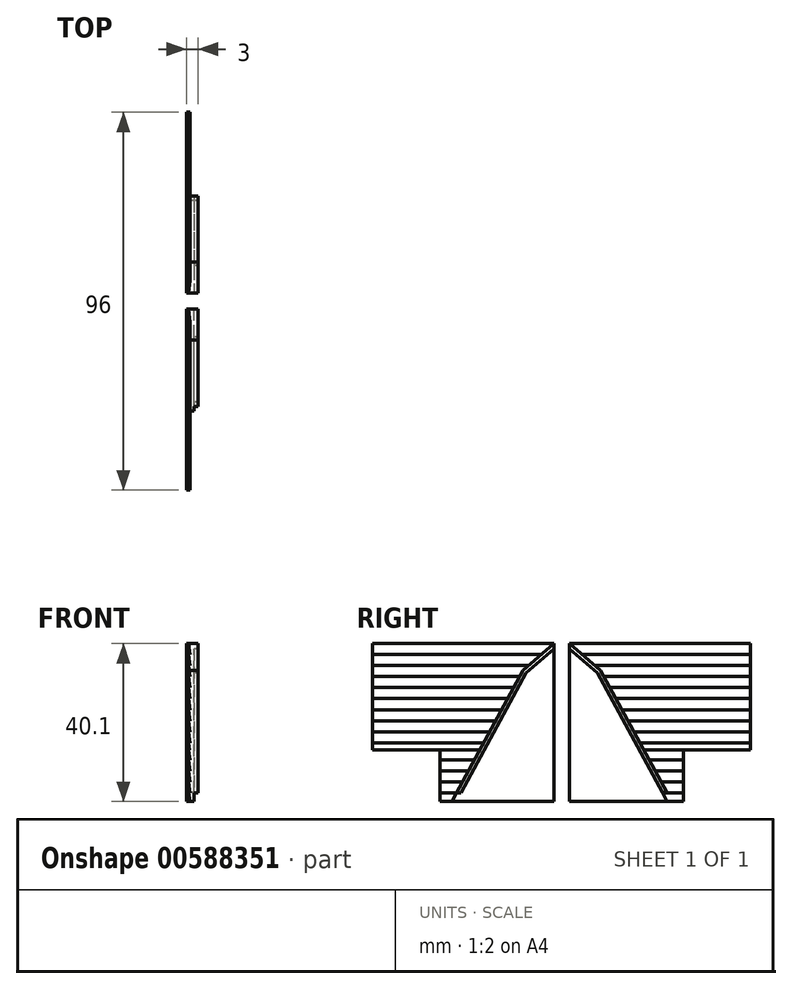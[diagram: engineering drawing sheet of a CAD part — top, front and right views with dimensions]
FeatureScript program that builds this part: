
annotation { "Feature Type Name" : "Feature", "Feature Type Description" : "" }
export const myFeature = defineFeature(function(context is Context, id is Id, definition is map)
    precondition{}
    {
        {
            var Q0;
            Q0=qCreatedBy(makeId("Right.planeOp"),FACE);
            var sketch = newSketch(context, id + "F0", { "sketchPlane" : qUnion([Q0])});
            skLineSegment(sketch, "E0", {"start": v(-104.3, 47.07) * mm, "end": v(-86.3, 47.07) * mm});
            skLineSegment(sketch, "E1", {"start": v(-104.3, 47.07) * mm, "end": v(-122.3, 47.07) * mm});
            skLineSegment(sketch, "E2", {"start": v(-86.3, 47.07) * mm, "end": v(-86.3, 33.97) * mm});
            skLineSegment(sketch, "E3", {"start": v(-122.3, 47.07) * mm, "end": v(-122.3, 33.97) * mm});
            skLineSegment(sketch, "E4", {"start": v(-122.3, 36.17) * mm, "end": v(-86.3, 36.17) * mm});
            skLineSegment(sketch, "E5", {"start": v(-86.3, 38.97) * mm, "end": v(-122.3, 38.97) * mm});
            skLineSegment(sketch, "E6", {"start": v(-122.3, 41.77) * mm, "end": v(-86.3, 41.77) * mm});
            skLineSegment(sketch, "E7", {"start": v(-86.3, 44.57) * mm, "end": v(-122.3, 44.57) * mm});
            skLineSegment(sketch, "E8", {"start": v(-122.3, 33.97) * mm, "end": v(-86.3, 33.97) * mm});
            skLineSegment(sketch, "E9", {"start": v(-86.3, 33.97) * mm, "end": v(-84.3, 33.97) * mm});
            skLineSegment(sketch, "E10.MirrorCS", {"start": v(-82.3, 33.97) * mm, "end": v(-84.3, 33.97) * mm});
            skLineSegment(sketch, "E11.MirrorCS", {"start": v(-64.3, 47.07) * mm, "end": v(-82.3, 47.07) * mm});
            skLineSegment(sketch, "E12.MirrorCS", {"start": v(-46.3, 47.07) * mm, "end": v(-46.3, 33.97) * mm});
            skLineSegment(sketch, "E13.MirrorCS", {"start": v(-82.3, 47.07) * mm, "end": v(-82.3, 33.97) * mm});
            skLineSegment(sketch, "E14.MirrorCS", {"start": v(-46.3, 36.17) * mm, "end": v(-82.3, 36.17) * mm});
            skLineSegment(sketch, "E15.MirrorCS", {"start": v(-46.3, 33.97) * mm, "end": v(-82.3, 33.97) * mm});
            skLineSegment(sketch, "E16.MirrorCS", {"start": v(-82.3, 44.57) * mm, "end": v(-46.3, 44.57) * mm});
            skLineSegment(sketch, "E17.MirrorCS", {"start": v(-64.3, 47.07) * mm, "end": v(-46.3, 47.07) * mm});
            skLineSegment(sketch, "E18.MirrorCS", {"start": v(-82.3, 38.97) * mm, "end": v(-46.3, 38.97) * mm});
            skLineSegment(sketch, "E19.MirrorCS", {"start": v(-46.3, 41.77) * mm, "end": v(-82.3, 41.77) * mm});
            skPoint(sketch, "E20.MirrorCS.end.orphan", {"position": v(-84.3, 47.07) * mm});
            skLineSegment(sketch, "E21", {"start": v(-86.3, 47.07) * mm, "end": v(-82.3, 47.07) * mm});
            skLineSegment(sketch, "E22", {"start": v(-86.3, 47.07) * mm, "end": v(-86.3, 48.87) * mm});
            skLineSegment(sketch, "E23", {"start": v(-86.3, 48.87) * mm, "end": v(-125.5, 48.87) * mm});
            skLineSegment(sketch, "E24", {"start": v(-125.5, 48.87) * mm, "end": v(-125.5, 51.9) * mm});
            skLineSegment(sketch, "E25", {"start": v(-122.3, 47.07) * mm, "end": v(-122.3, 48.87) * mm});
            skLineSegment(sketch, "E26", {"start": v(-122.3, 48.87) * mm, "end": v(-122.3, 51.67) * mm});
            skLineSegment(sketch, "E27", {"start": v(-122.3, 51.67) * mm, "end": v(-122.3, 54.47) * mm});
            skLineSegment(sketch, "E28", {"start": v(-122.3, 54.47) * mm, "end": v(-122.3, 57.27) * mm});
            skLineSegment(sketch, "E29", {"start": v(-122.3, 57.27) * mm, "end": v(-122.3, 60.07) * mm});
            skLineSegment(sketch, "E30", {"start": v(-122.3, 60.07) * mm, "end": v(-122.3, 62.87) * mm});
            skLineSegment(sketch, "E31", {"start": v(-122.3, 62.87) * mm, "end": v(-122.3, 65.67) * mm});
            skLineSegment(sketch, "E32", {"start": v(-122.3, 65.67) * mm, "end": v(-122.3, 68.47) * mm});
            skLineSegment(sketch, "E33", {"start": v(-122.3, 68.47) * mm, "end": v(-122.3, 71.27) * mm});
            skLineSegment(sketch, "E34", {"start": v(-122.3, 71.27) * mm, "end": v(-122.3, 74.07) * mm});
            skLineSegment(sketch, "E35", {"start": v(-122.3, 74.07) * mm, "end": v(-122.3, 76.87) * mm});
            skLineSegment(sketch, "E36", {"start": v(-122.3, 76.87) * mm, "end": v(-122.3, 79.67) * mm});
            skLineSegment(sketch, "E37", {"start": v(-122.3, 79.67) * mm, "end": v(-86.3, 79.67) * mm});
            skLineSegment(sketch, "E38", {"start": v(-86.3, 79.67) * mm, "end": v(-86.3, 48.87) * mm});
            skLineSegment(sketch, "E39", {"start": v(-86.3, 79.67) * mm, "end": v(-82.3, 79.67) * mm});
            skLineSegment(sketch, "E40", {"start": v(-82.3, 79.67) * mm, "end": v(-82.3, 47.07) * mm});
            skLineSegment(sketch, "E41", {"start": v(-82.3, 79.67) * mm, "end": v(-46.3, 79.67) * mm});
            skLineSegment(sketch, "E42", {"start": v(-46.3, 79.67) * mm, "end": v(-46.3, 47.07) * mm});
            skLineSegment(sketch, "E43", {"start": v(-46.3, 79.67) * mm, "end": v(-36.3, 79.67) * mm});
            skLineSegment(sketch, "E44", {"start": v(-46.3, 47.07) * mm, "end": v(-36.3, 47.07) * mm});
            skLineSegment(sketch, "E45", {"start": v(-36.3, 47.07) * mm, "end": v(-36.3, 79.67) * mm});
            skLineSegment(sketch, "E46", {"start": v(-122.3, 79.67) * mm, "end": v(-132.3, 79.67) * mm});
            skLineSegment(sketch, "E47", {"start": v(-122.3, 47.07) * mm, "end": v(-132.3, 47.07) * mm});
            skLineSegment(sketch, "E48", {"start": v(-132.3, 47.07) * mm, "end": v(-132.3, 79.67) * mm});
            skLineSegment(sketch, "E49", {"start": v(-190.64, 79.26) * mm, "end": v(-172.64, 45.96) * mm});
            skLineSegment(sketch, "E50", {"start": v(-220.64, 104.51) * mm, "end": v(-190.64, 79.26) * mm});
            skLineSegment(sketch, "E51", {"start": v(-172.64, 45.96) * mm, "end": v(-169.64, 45.96) * mm});
            skLineSegment(sketch, "E52", {"start": v(-172.64, 45.96) * mm, "end": v(-217.16, 45.96) * mm});
            skLineSegment(sketch, "E53", {"start": v(-190.64, 79.26) * mm, "end": v(-227.63, 79.26) * mm});
            skSolve(sketch);
        }
        {
            var Q0;
            {var subQ2=sQuery(id+"F0.wireOp",EDGE,"E4");Q0=makeQuery(id+"F0.imprint","IMPRINT",FACE,{"disambiguationData":[TD([[makeQuery(id+"F0.imprint","IMPRINT",EDGE,{"derivedFrom":subQ2}),-1.0]])]});}
            extrude(context, id + "F1", {"entities" : qUnion([Q0]), "depth" : 1 * mm, "offsetDistance" : 25 * mm});
        }
        {
            var Q0;
            Q0=makeQuery(id+"F1.opExtrude","SWEPT_FACE",FACE,{"disambiguationData":[OSD([sQuery(id+"F0.wireOp",EDGE,"E3")])]});
            var sketch = newSketch(context, id + "F2", { "sketchPlane" : qUnion([Q0])});
            skLineSegment(sketch, "E54", {"start": v(0, 33.97) * mm, "end": v(0, 36.17) * mm});
            skLineSegment(sketch, "E55", {"start": v(0, 36.17) * mm, "end": v(0, 33.37) * mm});
            skLineSegment(sketch, "E56", {"start": v(0, 33.37) * mm, "end": v(1, 33.37) * mm});
            skLineSegment(sketch, "E57", {"start": v(1, 36.17) * mm, "end": v(1, 33.37) * mm});
            skLineSegment(sketch, "E58", {"start": v(0, 38.97) * mm, "end": v(0, 36.17) * mm});
            skLineSegment(sketch, "E59", {"start": v(0, 33.37) * mm, "end": v(0.5, 33.37) * mm});
            skLineSegment(sketch, "E60", {"start": v(0, 36.17) * mm, "end": v(0.5, 36.17) * mm});
            skLineSegment(sketch, "E61", {"start": v(0.5, 36.17) * mm, "end": v(1, 33.37) * mm});
            skLineSegment(sketch, "E62", {"start": v(0, 38.97) * mm, "end": v(0.5, 38.97) * mm});
            skLineSegment(sketch, "E63", {"start": v(0.5, 38.97) * mm, "end": v(1, 36.17) * mm});
            skLineSegment(sketch, "E64", {"start": v(0.5, 38.97) * mm, "end": v(1, 38.97) * mm});
            skLineSegment(sketch, "E65", {"start": v(0, 38.97) * mm, "end": v(0, 41.77) * mm});
            skLineSegment(sketch, "E66", {"start": v(0, 41.77) * mm, "end": v(0.5, 41.77) * mm});
            skLineSegment(sketch, "E67", {"start": v(0.5, 41.77) * mm, "end": v(1, 41.77) * mm});
            skLineSegment(sketch, "E68", {"start": v(0.5, 41.77) * mm, "end": v(1, 38.97) * mm});
            skLineSegment(sketch, "E69", {"start": v(0, 41.77) * mm, "end": v(0, 44.57) * mm});
            skLineSegment(sketch, "E70", {"start": v(0, 44.57) * mm, "end": v(0.5, 44.57) * mm});
            skLineSegment(sketch, "E71", {"start": v(0.5, 44.57) * mm, "end": v(1, 44.57) * mm});
            skLineSegment(sketch, "E72", {"start": v(1, 41.77) * mm, "end": v(0.5, 44.57) * mm});
            skLineSegment(sketch, "E73", {"start": v(0, 44.57) * mm, "end": v(0, 47.07) * mm});
            skLineSegment(sketch, "E74", {"start": v(0, 47.07) * mm, "end": v(0.5, 47.07) * mm});
            skLineSegment(sketch, "E75", {"start": v(0.5, 47.07) * mm, "end": v(0.82, 47.07) * mm});
            skLineSegment(sketch, "E76", {"start": v(1, 44.57) * mm, "end": v(0.5, 47.07) * mm});
            skLineSegment(sketch, "E77", {"start": v(0, 47.07) * mm, "end": v(0, 48.87) * mm});
            skLineSegment(sketch, "E78", {"start": v(0, 48.87) * mm, "end": v(0.5, 48.87) * mm});
            skLineSegment(sketch, "E79", {"start": v(0.5, 48.87) * mm, "end": v(1, 48.87) * mm});
            skLineSegment(sketch, "E80", {"start": v(0, 48.87) * mm, "end": v(0, 51.67) * mm});
            skLineSegment(sketch, "E81", {"start": v(0, 51.67) * mm, "end": v(0.5, 51.67) * mm});
            skLineSegment(sketch, "E82", {"start": v(0.5, 51.67) * mm, "end": v(1, 51.67) * mm});
            skLineSegment(sketch, "E83", {"start": v(0, 51.67) * mm, "end": v(0, 54.47) * mm});
            skLineSegment(sketch, "E84", {"start": v(0, 54.47) * mm, "end": v(0.5, 54.47) * mm});
            skLineSegment(sketch, "E85", {"start": v(0.5, 54.47) * mm, "end": v(1, 54.47) * mm});
            skLineSegment(sketch, "E86", {"start": v(0, 54.47) * mm, "end": v(0, 57.27) * mm});
            skLineSegment(sketch, "E87", {"start": v(0, 57.27) * mm, "end": v(0.5, 57.27) * mm});
            skLineSegment(sketch, "E88", {"start": v(0.5, 57.27) * mm, "end": v(1, 57.27) * mm});
            skLineSegment(sketch, "E89", {"start": v(0, 57.27) * mm, "end": v(0, 60.07) * mm});
            skLineSegment(sketch, "E90", {"start": v(0, 60.07) * mm, "end": v(0.5, 60.07) * mm});
            skLineSegment(sketch, "E91", {"start": v(0.5, 60.07) * mm, "end": v(1, 60.07) * mm});
            skLineSegment(sketch, "E92", {"start": v(0, 60.07) * mm, "end": v(0, 62.87) * mm});
            skLineSegment(sketch, "E93", {"start": v(0, 62.87) * mm, "end": v(0.5, 62.87) * mm});
            skLineSegment(sketch, "E94", {"start": v(0.5, 62.87) * mm, "end": v(1, 62.87) * mm});
            skLineSegment(sketch, "E95", {"start": v(0, 62.87) * mm, "end": v(0, 65.67) * mm});
            skLineSegment(sketch, "E96", {"start": v(0, 65.67) * mm, "end": v(0.5, 65.67) * mm});
            skLineSegment(sketch, "E97", {"start": v(0.5, 65.67) * mm, "end": v(1, 65.67) * mm});
            skLineSegment(sketch, "E98", {"start": v(0, 65.67) * mm, "end": v(0, 68.47) * mm});
            skLineSegment(sketch, "E99", {"start": v(0, 68.47) * mm, "end": v(0.5, 68.47) * mm});
            skLineSegment(sketch, "E100", {"start": v(0.5, 68.47) * mm, "end": v(1, 68.47) * mm});
            skLineSegment(sketch, "E101", {"start": v(0, 68.47) * mm, "end": v(0, 71.27) * mm});
            skLineSegment(sketch, "E102", {"start": v(0, 71.27) * mm, "end": v(0.5, 71.27) * mm});
            skLineSegment(sketch, "E103", {"start": v(0.5, 71.27) * mm, "end": v(1, 71.27) * mm});
            skLineSegment(sketch, "E104", {"start": v(0, 71.27) * mm, "end": v(0, 74.07) * mm});
            skLineSegment(sketch, "E105", {"start": v(0, 74.07) * mm, "end": v(0.5, 74.07) * mm});
            skLineSegment(sketch, "E106", {"start": v(0.5, 74.07) * mm, "end": v(1, 74.07) * mm});
            skLineSegment(sketch, "E107", {"start": v(0, 74.07) * mm, "end": v(0, 76.87) * mm});
            skLineSegment(sketch, "E108", {"start": v(0, 76.87) * mm, "end": v(0.5, 76.87) * mm});
            skLineSegment(sketch, "E109", {"start": v(0.5, 76.87) * mm, "end": v(1, 76.87) * mm});
            skLineSegment(sketch, "E110", {"start": v(0, 76.87) * mm, "end": v(0, 79.67) * mm});
            skLineSegment(sketch, "E111", {"start": v(0, 79.67) * mm, "end": v(0.5, 79.67) * mm});
            skLineSegment(sketch, "E112", {"start": v(0.5, 74.07) * mm, "end": v(1, 71.27) * mm});
            skLineSegment(sketch, "E113", {"start": v(0.5, 71.27) * mm, "end": v(1, 68.47) * mm});
            skLineSegment(sketch, "E114", {"start": v(0.5, 68.47) * mm, "end": v(1, 65.67) * mm});
            skLineSegment(sketch, "E115", {"start": v(0.5, 65.67) * mm, "end": v(1, 62.87) * mm});
            skLineSegment(sketch, "E116", {"start": v(0.5, 62.87) * mm, "end": v(1, 60.07) * mm});
            skLineSegment(sketch, "E117", {"start": v(0.5, 60.07) * mm, "end": v(1, 57.27) * mm});
            skLineSegment(sketch, "E118", {"start": v(0.5, 57.27) * mm, "end": v(1, 54.47) * mm});
            skLineSegment(sketch, "E119", {"start": v(0.5, 54.47) * mm, "end": v(1, 51.67) * mm});
            skLineSegment(sketch, "E120", {"start": v(0.5, 51.67) * mm, "end": v(1, 48.87) * mm});
            skLineSegment(sketch, "E121", {"start": v(0.82, 47.07) * mm, "end": v(0.5, 48.87) * mm});
            skLineSegment(sketch, "E122", {"start": v(0.5, 36.17) * mm, "end": v(1, 36.17) * mm});
            skSolve(sketch);
        }
        {
            var Q0;
            {var subQ0=sQuery(id+"F2.wireOp",EDGE,"E57");var subQ1=sQuery(id+"F0.wireOp",EDGE,"E3");var subQ2=makeQuery(id+"F1.opExtrude","SWEPT_EDGE",EDGE,{"disambiguationData":[OSD([subQ1,sQuery(id+"F0.wireOp",EDGE,"E8")])]});var subQ3=makeQuery(id+"F2.imprint","INTERSECT",VERTEX,{"derivedFrom":[subQ2,subQ0]});Q0=makeQuery(id+"F2.imprint","IMPRINT",FACE,{"disambiguationData":[TD([[makeQuery(id+"F2.imprint","IMPRINT",EDGE,{"disambiguationData":[TD([[subQ3,1.0]])],"derivedFrom":subQ0}),-1.0]])]});}
            extrude(context, id + "F3", {"entities" : qUnion([Q0]), "operationType" : NewBodyOperationType.REMOVE, "oppositeDirection" : true, "depth" : 50 * mm, "offsetDistance" : 25 * mm});
        }
        {
            var Q0;
            Q0=makeQuery(id+"F1.opExtrude","SWEPT_FACE",FACE,{"disambiguationData":[OSD([sQuery(id+"F0.wireOp",EDGE,"E2")])]});
            extrude(context, id + "F4", {"entities" : qUnion([Q0]), "operationType" : NewBodyOperationType.ADD, "depth" : 40 * mm, "offsetDistance" : 25 * mm});
        }
        {
            var Q0;
            Q0=makeQuery(id+"F2.imprint","IMPRINT",FACE,{"disambiguationData":[TD([[makeQuery(id+"F2.imprint","IMPRINT",EDGE,{"derivedFrom":sQuery(id+"F2.wireOp",EDGE,"E58")}),1.0]])]});
            var Q1;
            Q1=makeQuery(id+"F2.imprint","IMPRINT",FACE,{"disambiguationData":[TD([[makeQuery(id+"F2.imprint","IMPRINT",EDGE,{"derivedFrom":sQuery(id+"F2.wireOp",EDGE,"E62")}),1.0]])]});
            var Q2;
            Q2=makeQuery(id+"F2.imprint","IMPRINT",FACE,{"disambiguationData":[TD([[makeQuery(id+"F2.imprint","IMPRINT",EDGE,{"derivedFrom":sQuery(id+"F2.wireOp",EDGE,"E66")}),1.0]])]});
            var Q3;
            Q3=makeQuery(id+"F2.imprint","IMPRINT",FACE,{"disambiguationData":[TD([[makeQuery(id+"F2.imprint","IMPRINT",EDGE,{"derivedFrom":sQuery(id+"F2.wireOp",EDGE,"E70")}),1.0]])]});
            var Q4;
            Q4=makeQuery(id+"F2.imprint","IMPRINT",FACE,{"disambiguationData":[TD([[makeQuery(id+"F2.imprint","IMPRINT",EDGE,{"derivedFrom":sQuery(id+"F2.wireOp",EDGE,"E74")}),1.0]])]});
            var Q5;
            Q5=makeQuery(id+"F2.imprint","IMPRINT",FACE,{"disambiguationData":[TD([[makeQuery(id+"F2.imprint","IMPRINT",EDGE,{"derivedFrom":sQuery(id+"F2.wireOp",EDGE,"E78")}),1.0]])]});
            var Q6;
            Q6=makeQuery(id+"F2.imprint","IMPRINT",FACE,{"disambiguationData":[TD([[makeQuery(id+"F2.imprint","IMPRINT",EDGE,{"derivedFrom":sQuery(id+"F2.wireOp",EDGE,"E81")}),1.0]])]});
            var Q7;
            Q7=makeQuery(id+"F2.imprint","IMPRINT",FACE,{"disambiguationData":[TD([[makeQuery(id+"F2.imprint","IMPRINT",EDGE,{"derivedFrom":sQuery(id+"F2.wireOp",EDGE,"E84")}),1.0]])]});
            var Q8;
            Q8=makeQuery(id+"F2.imprint","IMPRINT",FACE,{"disambiguationData":[TD([[makeQuery(id+"F2.imprint","IMPRINT",EDGE,{"derivedFrom":sQuery(id+"F2.wireOp",EDGE,"E87")}),1.0]])]});
            var Q9;
            Q9=makeQuery(id+"F2.imprint","IMPRINT",FACE,{"disambiguationData":[TD([[makeQuery(id+"F2.imprint","IMPRINT",EDGE,{"derivedFrom":sQuery(id+"F2.wireOp",EDGE,"E90")}),1.0]])]});
            var Q10;
            Q10=makeQuery(id+"F2.imprint","IMPRINT",FACE,{"disambiguationData":[TD([[makeQuery(id+"F2.imprint","IMPRINT",EDGE,{"derivedFrom":sQuery(id+"F2.wireOp",EDGE,"E93")}),1.0]])]});
            var Q11;
            Q11=makeQuery(id+"F2.imprint","IMPRINT",FACE,{"disambiguationData":[TD([[makeQuery(id+"F2.imprint","IMPRINT",EDGE,{"derivedFrom":sQuery(id+"F2.wireOp",EDGE,"E96")}),1.0]])]});
            var Q12;
            Q12=makeQuery(id+"F2.imprint","IMPRINT",FACE,{"disambiguationData":[TD([[makeQuery(id+"F2.imprint","IMPRINT",EDGE,{"derivedFrom":sQuery(id+"F2.wireOp",EDGE,"E99")}),1.0]])]});
            var Q13;
            Q13=makeQuery(id+"F2.imprint","IMPRINT",FACE,{"disambiguationData":[TD([[makeQuery(id+"F2.imprint","IMPRINT",EDGE,{"derivedFrom":sQuery(id+"F2.wireOp",EDGE,"E102")}),1.0]])]});
            var Q14;
            Q14=makeQuery(id+"F2.imprint","IMPRINT",FACE,{"disambiguationData":[TD([[makeQuery(id+"F2.imprint","IMPRINT",EDGE,{"derivedFrom":sQuery(id+"F2.wireOp",EDGE,"E105")}),1.0]])]});
            var Q15;
            Q15=makeQuery(id+"F2.imprint","IMPRINT",FACE,{"disambiguationData":[TD([[makeQuery(id+"F2.imprint","IMPRINT",EDGE,{"derivedFrom":sQuery(id+"F2.wireOp",EDGE,"E108")}),1.0]])]});
            extrude(context, id + "F5", {"entities" : qUnion([Q0, Q1, Q2, Q3, Q4, Q5, Q6, Q7, Q8, Q9, Q10, Q11, Q12, Q13, Q14, Q15]), "operationType" : NewBodyOperationType.ADD, "oppositeDirection" : true, "depth" : 76 * mm, "offsetDistance" : 25 * mm});
        }
        {
            var Q0;
            Q0=makeQuery(id+"F0.imprint","IMPRINT",FACE,{"disambiguationData":[TD([[makeQuery(id+"F0.imprint","IMPRINT",EDGE,{"derivedFrom":sQuery(id+"F0.wireOp",EDGE,"E21")}),1.0]])]});
            var Q1;
            {var subQ1=sQuery(id+"F0.wireOp",EDGE,"E9");Q1=makeQuery(id+"F0.imprint","IMPRINT",FACE,{"disambiguationData":[TD([[makeQuery(id+"F0.imprint","IMPRINT",EDGE,{"derivedFrom":subQ1}),1.0]])]});}
            extrude(context, id + "F6", {"entities" : qUnion([Q0, Q1]), "operationType" : NewBodyOperationType.REMOVE, "depth" : 25 * mm, "offsetDistance" : 25 * mm});
        }
        {
            var Q0;
            Q0=makeQuery(id+"F5.boolean.opBoolean","MERGE",FACE,{"derivedFrom":[makeQuery(id+"F4.opExtrude","CAP_FACE",FACE,{"disambiguationData":[OSD([sQuery(id+"F0.wireOp",EDGE,"E2")])],"isStart":false}),makeQuery(id+"F5.opExtrude","CAP_FACE",FACE,{"disambiguationData":[OSD([sQuery(id+"F2.wireOp",EDGE,"E58"),sQuery(id+"F2.wireOp",EDGE,"E60"),sQuery(id+"F2.wireOp",EDGE,"E63"),sQuery(id+"F2.wireOp",EDGE,"E64"),sQuery(id+"F2.wireOp",EDGE,"E65"),sQuery(id+"F2.wireOp",EDGE,"E67"),sQuery(id+"F2.wireOp",EDGE,"E68"),sQuery(id+"F2.wireOp",EDGE,"E69"),sQuery(id+"F2.wireOp",EDGE,"E71"),sQuery(id+"F2.wireOp",EDGE,"E72"),sQuery(id+"F2.wireOp",EDGE,"E73"),sQuery(id+"F2.wireOp",EDGE,"E75"),sQuery(id+"F2.wireOp",EDGE,"E76"),sQuery(id+"F2.wireOp",EDGE,"E77"),sQuery(id+"F2.wireOp",EDGE,"E79"),sQuery(id+"F2.wireOp",EDGE,"E80"),sQuery(id+"F2.wireOp",EDGE,"E82"),sQuery(id+"F2.wireOp",EDGE,"E83"),sQuery(id+"F2.wireOp",EDGE,"E85"),sQuery(id+"F2.wireOp",EDGE,"E86"),sQuery(id+"F2.wireOp",EDGE,"E88"),sQuery(id+"F2.wireOp",EDGE,"E89"),sQuery(id+"F2.wireOp",EDGE,"E91"),sQuery(id+"F2.wireOp",EDGE,"E92"),sQuery(id+"F2.wireOp",EDGE,"E94"),sQuery(id+"F2.wireOp",EDGE,"E95"),sQuery(id+"F2.wireOp",EDGE,"E97"),sQuery(id+"F2.wireOp",EDGE,"E98"),sQuery(id+"F2.wireOp",EDGE,"E100"),sQuery(id+"F2.wireOp",EDGE,"E101"),sQuery(id+"F2.wireOp",EDGE,"E103"),sQuery(id+"F2.wireOp",EDGE,"E104"),sQuery(id+"F2.wireOp",EDGE,"E105"),sQuery(id+"F2.wireOp",EDGE,"E112"),sQuery(id+"F2.wireOp",EDGE,"E113"),sQuery(id+"F2.wireOp",EDGE,"E114"),sQuery(id+"F2.wireOp",EDGE,"E115"),sQuery(id+"F2.wireOp",EDGE,"E116"),sQuery(id+"F2.wireOp",EDGE,"E117"),sQuery(id+"F2.wireOp",EDGE,"E118"),sQuery(id+"F2.wireOp",EDGE,"E119"),sQuery(id+"F2.wireOp",EDGE,"E120"),sQuery(id+"F2.wireOp",EDGE,"E121"),sQuery(id+"F2.wireOp",EDGE,"E122")])],"isStart":false})]});
            var sketch = newSketch(context, id + "F7", { "sketchPlane" : qUnion([Q0])});
            skLineSegment(sketch, "E123", {"start": v(-0.5, 47.07) * mm, "end": v(0, 47.07) * mm});
            skSolve(sketch);
        }
        {
            var Q0;
            {var subQ1=sQuery(id+"F7.wireOp",EDGE,"E123");Q0=makeQuery(id+"F7.imprint","IMPRINT",FACE,{"disambiguationData":[TD([[makeQuery(id+"F7.imprint","IMPRINT",EDGE,{"derivedFrom":subQ1}),1.0]])]});}
            extrude(context, id + "F8", {"entities" : qUnion([Q0]), "operationType" : NewBodyOperationType.ADD, "depth" : 10 * mm, "offsetDistance" : 25 * mm});
        }
        {
            var Q0;
            Q0=makeQuery(id+"F2.imprint","IMPRINT",FACE,{"disambiguationData":[TD([[makeQuery(id+"F2.imprint","IMPRINT",EDGE,{"derivedFrom":sQuery(id+"F2.wireOp",EDGE,"E102")}),1.0]])]});
            var Q1;
            Q1=makeQuery(id+"F2.imprint","IMPRINT",FACE,{"disambiguationData":[TD([[makeQuery(id+"F2.imprint","IMPRINT",EDGE,{"derivedFrom":sQuery(id+"F2.wireOp",EDGE,"E99")}),1.0]])]});
            var Q2;
            Q2=makeQuery(id+"F2.imprint","IMPRINT",FACE,{"disambiguationData":[TD([[makeQuery(id+"F2.imprint","IMPRINT",EDGE,{"derivedFrom":sQuery(id+"F2.wireOp",EDGE,"E96")}),1.0]])]});
            var Q3;
            Q3=makeQuery(id+"F2.imprint","IMPRINT",FACE,{"disambiguationData":[TD([[makeQuery(id+"F2.imprint","IMPRINT",EDGE,{"derivedFrom":sQuery(id+"F2.wireOp",EDGE,"E93")}),1.0]])]});
            var Q4;
            Q4=makeQuery(id+"F2.imprint","IMPRINT",FACE,{"disambiguationData":[TD([[makeQuery(id+"F2.imprint","IMPRINT",EDGE,{"derivedFrom":sQuery(id+"F2.wireOp",EDGE,"E90")}),1.0]])]});
            var Q5;
            Q5=makeQuery(id+"F2.imprint","IMPRINT",FACE,{"disambiguationData":[TD([[makeQuery(id+"F2.imprint","IMPRINT",EDGE,{"derivedFrom":sQuery(id+"F2.wireOp",EDGE,"E87")}),1.0]])]});
            var Q6;
            Q6=makeQuery(id+"F2.imprint","IMPRINT",FACE,{"disambiguationData":[TD([[makeQuery(id+"F2.imprint","IMPRINT",EDGE,{"derivedFrom":sQuery(id+"F2.wireOp",EDGE,"E84")}),1.0]])]});
            var Q7;
            Q7=makeQuery(id+"F2.imprint","IMPRINT",FACE,{"disambiguationData":[TD([[makeQuery(id+"F2.imprint","IMPRINT",EDGE,{"derivedFrom":sQuery(id+"F2.wireOp",EDGE,"E81")}),1.0]])]});
            var Q8;
            Q8=makeQuery(id+"F2.imprint","IMPRINT",FACE,{"disambiguationData":[TD([[makeQuery(id+"F2.imprint","IMPRINT",EDGE,{"derivedFrom":sQuery(id+"F2.wireOp",EDGE,"E78")}),1.0]])]});
            extrude(context, id + "F9", {"entities" : qUnion([Q0, Q1, Q2, Q3, Q4, Q5, Q6, Q7, Q8]), "operationType" : NewBodyOperationType.ADD, "depth" : 10 * mm, "offsetDistance" : 25 * mm});
        }
        {
            var Q0;
            Q0=makeQuery(id+"F5.boolean.opBoolean","MERGE",FACE,{"derivedFrom":[makeQuery(id+"F4.opExtrude","CAP_FACE",FACE,{"disambiguationData":[OSD([sQuery(id+"F0.wireOp",EDGE,"E2")])],"isStart":false}),makeQuery(id+"F5.opExtrude","CAP_FACE",FACE,{"disambiguationData":[OSD([sQuery(id+"F2.wireOp",EDGE,"E58"),sQuery(id+"F2.wireOp",EDGE,"E60"),sQuery(id+"F2.wireOp",EDGE,"E63"),sQuery(id+"F2.wireOp",EDGE,"E64"),sQuery(id+"F2.wireOp",EDGE,"E65"),sQuery(id+"F2.wireOp",EDGE,"E67"),sQuery(id+"F2.wireOp",EDGE,"E68"),sQuery(id+"F2.wireOp",EDGE,"E69"),sQuery(id+"F2.wireOp",EDGE,"E71"),sQuery(id+"F2.wireOp",EDGE,"E72"),sQuery(id+"F2.wireOp",EDGE,"E73"),sQuery(id+"F2.wireOp",EDGE,"E75"),sQuery(id+"F2.wireOp",EDGE,"E76"),sQuery(id+"F2.wireOp",EDGE,"E77"),sQuery(id+"F2.wireOp",EDGE,"E79"),sQuery(id+"F2.wireOp",EDGE,"E80"),sQuery(id+"F2.wireOp",EDGE,"E82"),sQuery(id+"F2.wireOp",EDGE,"E83"),sQuery(id+"F2.wireOp",EDGE,"E85"),sQuery(id+"F2.wireOp",EDGE,"E86"),sQuery(id+"F2.wireOp",EDGE,"E88"),sQuery(id+"F2.wireOp",EDGE,"E89"),sQuery(id+"F2.wireOp",EDGE,"E91"),sQuery(id+"F2.wireOp",EDGE,"E92"),sQuery(id+"F2.wireOp",EDGE,"E94"),sQuery(id+"F2.wireOp",EDGE,"E95"),sQuery(id+"F2.wireOp",EDGE,"E97"),sQuery(id+"F2.wireOp",EDGE,"E98"),sQuery(id+"F2.wireOp",EDGE,"E100"),sQuery(id+"F2.wireOp",EDGE,"E101"),sQuery(id+"F2.wireOp",EDGE,"E103"),sQuery(id+"F2.wireOp",EDGE,"E104"),sQuery(id+"F2.wireOp",EDGE,"E105"),sQuery(id+"F2.wireOp",EDGE,"E112"),sQuery(id+"F2.wireOp",EDGE,"E113"),sQuery(id+"F2.wireOp",EDGE,"E114"),sQuery(id+"F2.wireOp",EDGE,"E115"),sQuery(id+"F2.wireOp",EDGE,"E116"),sQuery(id+"F2.wireOp",EDGE,"E117"),sQuery(id+"F2.wireOp",EDGE,"E118"),sQuery(id+"F2.wireOp",EDGE,"E119"),sQuery(id+"F2.wireOp",EDGE,"E120"),sQuery(id+"F2.wireOp",EDGE,"E121"),sQuery(id+"F2.wireOp",EDGE,"E122")])],"isStart":false})]});
            extrude(context, id + "F10", {"entities" : qUnion([Q0]), "operationType" : NewBodyOperationType.ADD, "depth" : 2 * mm, "offsetDistance" : 25 * mm});
        }
        {
            var Q0;
            Q0=makeQuery(id+"F2.imprint","IMPRINT",FACE,{"disambiguationData":[TD([[makeQuery(id+"F2.imprint","IMPRINT",EDGE,{"derivedFrom":sQuery(id+"F2.wireOp",EDGE,"E74")}),1.0]])]});
            extrude(context, id + "F11", {"entities" : qUnion([Q0]), "operationType" : NewBodyOperationType.ADD, "depth" : 10 * mm, "offsetDistance" : 25 * mm});
        }
        {
            var Q0;
            Q0=makeQuery(id+"F2.imprint","IMPRINT",FACE,{"disambiguationData":[TD([[makeQuery(id+"F2.imprint","IMPRINT",EDGE,{"derivedFrom":sQuery(id+"F2.wireOp",EDGE,"E70")}),1.0]])]});
            var Q1;
            Q1=makeQuery(id+"F2.imprint","IMPRINT",FACE,{"disambiguationData":[TD([[makeQuery(id+"F2.imprint","IMPRINT",EDGE,{"derivedFrom":sQuery(id+"F2.wireOp",EDGE,"E66")}),1.0]])]});
            var Q2;
            Q2=makeQuery(id+"F2.imprint","IMPRINT",FACE,{"disambiguationData":[TD([[makeQuery(id+"F2.imprint","IMPRINT",EDGE,{"derivedFrom":sQuery(id+"F2.wireOp",EDGE,"E62")}),1.0]])]});
            var Q3;
            Q3=makeQuery(id+"F2.imprint","IMPRINT",FACE,{"disambiguationData":[TD([[makeQuery(id+"F2.imprint","IMPRINT",EDGE,{"derivedFrom":sQuery(id+"F2.wireOp",EDGE,"E58")}),1.0]])]});
            var Q4;
            {var subQ3=sQuery(id+"F2.wireOp",EDGE,"E60");Q4=makeQuery(id+"F2.imprint","IMPRINT",FACE,{"disambiguationData":[TD([[makeQuery(id+"F2.imprint","IMPRINT",EDGE,{"derivedFrom":subQ3}),1.0]])]});}
            extrude(context, id + "F12", {"entities" : qUnion([Q0, Q1, Q2, Q3, Q4]), "operationType" : NewBodyOperationType.ADD, "depth" : 2 * mm, "offsetDistance" : 25 * mm});
        }
        {
            var Q0;
            Q0=makeQuery(id+"F12.opExtrude","CAP_FACE",FACE,{"disambiguationData":[OSD([sQuery(id+"F0.wireOp",EDGE,"E3"),sQuery(id+"F0.wireOp",EDGE,"E8"),sQuery(id+"F2.wireOp",EDGE,"E55"),sQuery(id+"F2.wireOp",EDGE,"E58"),sQuery(id+"F2.wireOp",EDGE,"E61"),sQuery(id+"F2.wireOp",EDGE,"E63"),sQuery(id+"F2.wireOp",EDGE,"E64"),sQuery(id+"F2.wireOp",EDGE,"E65"),sQuery(id+"F2.wireOp",EDGE,"E67"),sQuery(id+"F2.wireOp",EDGE,"E68"),sQuery(id+"F2.wireOp",EDGE,"E69"),sQuery(id+"F2.wireOp",EDGE,"E71"),sQuery(id+"F2.wireOp",EDGE,"E72"),sQuery(id+"F2.wireOp",EDGE,"E73"),sQuery(id+"F2.wireOp",EDGE,"E74"),sQuery(id+"F2.wireOp",EDGE,"E76"),sQuery(id+"F2.wireOp",EDGE,"E122")])],"isStart":false});
            extrude(context, id + "F13", {"entities" : qUnion([Q0]), "operationType" : NewBodyOperationType.REMOVE, "oppositeDirection" : true, "depth" : 9.1 * mm, "offsetDistance" : 25 * mm});
        }
        {
            var Q0;
            Q0=makeQuery(id+"F10.opExtrude","CAP_FACE",FACE,{"disambiguationData":[OSD([sQuery(id+"F0.wireOp",EDGE,"E2"),sQuery(id+"F2.wireOp",EDGE,"E58"),sQuery(id+"F2.wireOp",EDGE,"E60"),sQuery(id+"F2.wireOp",EDGE,"E63"),sQuery(id+"F2.wireOp",EDGE,"E64"),sQuery(id+"F2.wireOp",EDGE,"E65"),sQuery(id+"F2.wireOp",EDGE,"E67"),sQuery(id+"F2.wireOp",EDGE,"E68"),sQuery(id+"F2.wireOp",EDGE,"E69"),sQuery(id+"F2.wireOp",EDGE,"E71"),sQuery(id+"F2.wireOp",EDGE,"E72"),sQuery(id+"F2.wireOp",EDGE,"E73"),sQuery(id+"F2.wireOp",EDGE,"E75"),sQuery(id+"F2.wireOp",EDGE,"E76"),sQuery(id+"F2.wireOp",EDGE,"E77"),sQuery(id+"F2.wireOp",EDGE,"E79"),sQuery(id+"F2.wireOp",EDGE,"E80"),sQuery(id+"F2.wireOp",EDGE,"E82"),sQuery(id+"F2.wireOp",EDGE,"E83"),sQuery(id+"F2.wireOp",EDGE,"E85"),sQuery(id+"F2.wireOp",EDGE,"E86"),sQuery(id+"F2.wireOp",EDGE,"E88"),sQuery(id+"F2.wireOp",EDGE,"E89"),sQuery(id+"F2.wireOp",EDGE,"E91"),sQuery(id+"F2.wireOp",EDGE,"E92"),sQuery(id+"F2.wireOp",EDGE,"E94"),sQuery(id+"F2.wireOp",EDGE,"E95"),sQuery(id+"F2.wireOp",EDGE,"E97"),sQuery(id+"F2.wireOp",EDGE,"E98"),sQuery(id+"F2.wireOp",EDGE,"E100"),sQuery(id+"F2.wireOp",EDGE,"E101"),sQuery(id+"F2.wireOp",EDGE,"E103"),sQuery(id+"F2.wireOp",EDGE,"E104"),sQuery(id+"F2.wireOp",EDGE,"E105"),sQuery(id+"F2.wireOp",EDGE,"E112"),sQuery(id+"F2.wireOp",EDGE,"E113"),sQuery(id+"F2.wireOp",EDGE,"E114"),sQuery(id+"F2.wireOp",EDGE,"E115"),sQuery(id+"F2.wireOp",EDGE,"E116"),sQuery(id+"F2.wireOp",EDGE,"E117"),sQuery(id+"F2.wireOp",EDGE,"E118"),sQuery(id+"F2.wireOp",EDGE,"E119"),sQuery(id+"F2.wireOp",EDGE,"E120"),sQuery(id+"F2.wireOp",EDGE,"E121"),sQuery(id+"F2.wireOp",EDGE,"E122")])],"isStart":false});
            extrude(context, id + "F14", {"entities" : qUnion([Q0]), "operationType" : NewBodyOperationType.REMOVE, "oppositeDirection" : true, "depth" : 9.1 * mm, "offsetDistance" : 25 * mm});
        }
        {
            var Q0;
            {var subQ2=sQuery(id+"F0.wireOp",EDGE,"E26");Q0=makeQuery(id+"F0.imprint","IMPRINT",FACE,{"disambiguationData":[TD([[makeQuery(id+"F0.imprint","IMPRINT",EDGE,{"derivedFrom":subQ2}),-1.0]])]});}
            var sketch = newSketch(context, id + "F15", { "sketchPlane" : qUnion([Q0])});
            skLineSegment(sketch, "E124.0", {"start": v(-86.3, 79.67) * mm, "end": v(-86.3, 48.87) * mm});
            skLineSegment(sketch, "E125.0", {"start": v(-86.3, 74.07) * mm, "end": v(-132.3, 74.07) * mm});
            skLineSegment(sketch, "E126.0", {"start": v(-132.3, 47.07) * mm, "end": v(-132.3, 79.67) * mm});
            skLineSegment(sketch, "E127.0", {"start": v(-122.3, 47.07) * mm, "end": v(-132.3, 47.07) * mm});
            skLineSegment(sketch, "E128.0", {"start": v(-104.3, 47.07) * mm, "end": v(-122.3, 47.07) * mm});
            skLineSegment(sketch, "E129.0", {"start": v(-115.2, 33.97) * mm, "end": v(-115.2, 47.07) * mm});
            skLineSegment(sketch, "E130.0", {"start": v(-122.3, 33.97) * mm, "end": v(-86.3, 33.97) * mm});
            skLineSegment(sketch, "E131.0", {"start": v(-86.3, 47.07) * mm, "end": v(-86.3, 33.97) * mm});
            skLineSegment(sketch, "E132.0", {"start": v(-86.3, 47.07) * mm, "end": v(-86.3, 48.87) * mm});
            skLineSegment(sketch, "E133", {"start": v(-115.2, 33.97) * mm, "end": v(-112.2, 33.97) * mm});
            skLineSegment(sketch, "E134", {"start": v(-112.2, 33.97) * mm, "end": v(-94.2, 67.27) * mm});
            skLineSegment(sketch, "E135.0", {"start": v(-86.3, 48.87) * mm, "end": v(-125.5, 48.87) * mm});
            skLineSegment(sketch, "E136.0", {"start": v(-104.3, 47.07) * mm, "end": v(-86.3, 47.07) * mm});
            skLineSegment(sketch, "E137.0", {"start": v(-86.3, 44.57) * mm, "end": v(-122.3, 44.57) * mm});
            skLineSegment(sketch, "E138.0", {"start": v(-122.3, 41.77) * mm, "end": v(-86.3, 41.77) * mm});
            skLineSegment(sketch, "E139.0", {"start": v(-86.3, 38.97) * mm, "end": v(-122.3, 38.97) * mm});
            skLineSegment(sketch, "E140.0", {"start": v(-122.3, 36.17) * mm, "end": v(-86.3, 36.17) * mm});
            skLineSegment(sketch, "E141", {"start": v(-94.2, 67.27) * mm, "end": v(-86.3, 74.07) * mm});
            skLineSegment(sketch, "E142.0", {"start": v(-93.4, 66.63) * mm, "end": v(-85.65, 73.3) * mm});
            skLineSegment(sketch, "E142.1", {"start": v(-111.32, 33.5) * mm, "end": v(-93.4, 66.63) * mm});
            skLineSegment(sketch, "E143", {"start": v(-86.3, 74.07) * mm, "end": v(-86.3, 72.75) * mm});
            skLineSegment(sketch, "E144", {"start": v(-112.2, 33.97) * mm, "end": v(-111.06, 33.97) * mm});
            skSolve(sketch);
        }
        {
            var Q0;
            {var subQ3=sQuery(id+"F15.wireOp",EDGE,"3uRzxeQ8-baQP-kUuA-5wLP-CMvW5qUhLGsQ");var subQ5=sQuery(id+"F15.wireOp",EDGE,"E134");var subQ6=makeQuery(id+"F15.imprint","INTERSECT",VERTEX,{"derivedFrom":[subQ5,subQ3]});Q0=makeQuery(id+"F15.imprint","IMPRINT",FACE,{"disambiguationData":[TD([[makeQuery(id+"F15.imprint","IMPRINT",EDGE,{"disambiguationData":[TD([[subQ6,1.0]])],"derivedFrom":subQ5}),-1.0]])]});}
            var Q1;
            {var subQ5=sQuery(id+"F15.wireOp",EDGE,"E132.0");Q1=makeQuery(id+"F15.imprint","IMPRINT",FACE,{"disambiguationData":[TD([[makeQuery(id+"F15.imprint","IMPRINT",EDGE,{"derivedFrom":subQ5}),1.0]])]});}
            var Q2;
            {var subQ0=sQuery(id+"F15.wireOp",EDGE,"E136.0");Q2=makeQuery(id+"F15.imprint","IMPRINT",FACE,{"disambiguationData":[TD([[makeQuery(id+"F15.imprint","IMPRINT",EDGE,{"derivedFrom":subQ0}),-1.0]])]});}
            var Q3;
            {var subQ0=sQuery(id+"F15.wireOp",EDGE,"E137.0");var subQ1=sQuery(id+"F15.wireOp",EDGE,"E131.0");var subQ2=makeQuery(id+"F15.imprint","INTERSECT",VERTEX,{"derivedFrom":[subQ1,subQ0]});Q3=makeQuery(id+"F15.imprint","IMPRINT",FACE,{"disambiguationData":[TD([[makeQuery(id+"F15.imprint","IMPRINT",EDGE,{"disambiguationData":[TD([[subQ2,-1.0]])],"derivedFrom":subQ1}),-1.0]])]});}
            var Q4;
            {var subQ0=sQuery(id+"F15.wireOp",EDGE,"E138.0");var subQ1=sQuery(id+"F15.wireOp",EDGE,"E131.0");var subQ2=makeQuery(id+"F15.imprint","INTERSECT",VERTEX,{"derivedFrom":[subQ1,subQ0]});Q4=makeQuery(id+"F15.imprint","IMPRINT",FACE,{"disambiguationData":[TD([[makeQuery(id+"F15.imprint","IMPRINT",EDGE,{"disambiguationData":[TD([[subQ2,-1.0]])],"derivedFrom":subQ1}),-1.0]])]});}
            var Q5;
            {var subQ0=sQuery(id+"F15.wireOp",EDGE,"E139.0");var subQ1=sQuery(id+"F15.wireOp",EDGE,"E131.0");var subQ2=makeQuery(id+"F15.imprint","INTERSECT",VERTEX,{"derivedFrom":[subQ1,subQ0]});Q5=makeQuery(id+"F15.imprint","IMPRINT",FACE,{"disambiguationData":[TD([[makeQuery(id+"F15.imprint","IMPRINT",EDGE,{"disambiguationData":[TD([[subQ2,-1.0]])],"derivedFrom":subQ1}),-1.0]])]});}
            var Q6;
            {var subQ0=sQuery(id+"F15.wireOp",EDGE,"E131.0");var subQ1=sQuery(id+"F15.wireOp",EDGE,"E130.0");var subQ2=makeQuery(id+"F15.imprint","INTERSECT",VERTEX,{"derivedFrom":[subQ1,subQ0]});Q6=makeQuery(id+"F15.imprint","IMPRINT",FACE,{"disambiguationData":[TD([[makeQuery(id+"F15.imprint","IMPRINT",EDGE,{"disambiguationData":[TD([[subQ2,1.0]])],"derivedFrom":subQ0}),-1.0]])]});}
            extrude(context, id + "F16", {"entities" : qUnion([Q0, Q1, Q2, Q3, Q4, Q5, Q6]), "operationType" : NewBodyOperationType.ADD, "depth" : 4 * mm, "offsetDistance" : 25 * mm});
        }
        {
            var Q0;
            Q0=makeQuery(id+"F16.opExtrude","CAP_FACE",FACE,{"disambiguationData":[OSD([sQuery(id+"F15.wireOp",EDGE,"E124.0"),sQuery(id+"F15.wireOp",EDGE,"E130.0"),sQuery(id+"F15.wireOp",EDGE,"E131.0"),sQuery(id+"F15.wireOp",EDGE,"E132.0"),sQuery(id+"F15.wireOp",EDGE,"E134"),sQuery(id+"F15.wireOp",EDGE,"3uRzxeQ8-baQP-kUuA-5wLP-CMvW5qUhLGsQ")])],"isStart":false});
            extrude(context, id + "F17", {"entities" : qUnion([Q0]), "operationType" : NewBodyOperationType.REMOVE, "oppositeDirection" : true, "depth" : 2 * mm, "offsetDistance" : 25 * mm});
        }
        {
            var Q0;
            Q0=makeQuery(id+"F0.imprint","IMPRINT",FACE,{"disambiguationData":[TD([[makeQuery(id+"F0.imprint","IMPRINT",EDGE,{"derivedFrom":sQuery(id+"F0.wireOp",EDGE,"E11.MirrorCS")}),-1.0]])]});
            var sketch = newSketch(context, id + "F18", { "sketchPlane" : qUnion([Q0])});
            skLineSegment(sketch, "E145.0", {"start": v(-46.3, 47.07) * mm, "end": v(-36.3, 47.07) * mm});
            skLineSegment(sketch, "E146.0", {"start": v(-64.3, 47.07) * mm, "end": v(-46.3, 47.07) * mm});
            skLineSegment(sketch, "E147.0", {"start": v(-36.3, 47.07) * mm, "end": v(-36.3, 79.67) * mm});
            skLineSegment(sketch, "E148.0", {"start": v(-36.3, 74.07) * mm, "end": v(-82.3, 74.07) * mm});
            skLineSegment(sketch, "E149.0", {"start": v(-82.3, 79.67) * mm, "end": v(-82.3, 47.07) * mm});
            skLineSegment(sketch, "E150.0", {"start": v(-53.4, 47.07) * mm, "end": v(-53.4, 33.97) * mm});
            skLineSegment(sketch, "E151.0", {"start": v(-46.3, 33.97) * mm, "end": v(-82.3, 33.97) * mm});
            skLineSegment(sketch, "E152.0", {"start": v(-82.3, 47.07) * mm, "end": v(-82.3, 33.97) * mm});
            skLineSegment(sketch, "E153", {"start": v(-53.4, 33.97) * mm, "end": v(-56.4, 33.97) * mm});
            skLineSegment(sketch, "E154", {"start": v(-56.4, 33.97) * mm, "end": v(-74.4, 67.27) * mm});
            skLineSegment(sketch, "E155", {"start": v(-74.4, 67.27) * mm, "end": v(-82.3, 74.07) * mm});
            skLineSegment(sketch, "E156", {"start": v(-82.3, 47.07) * mm, "end": v(-63.49, 47.07) * mm});
            skLineSegment(sketch, "E157", {"start": v(-82.3, 33.97) * mm, "end": v(-82.3, 36.2) * mm});
            skLineSegment(sketch, "E158", {"start": v(-82.3, 36.2) * mm, "end": v(-82.3, 39.01) * mm});
            skLineSegment(sketch, "E159", {"start": v(-82.3, 39.01) * mm, "end": v(-82.3, 41.78) * mm});
            skLineSegment(sketch, "E160", {"start": v(-82.3, 41.78) * mm, "end": v(-82.3, 44.63) * mm});
            skLineSegment(sketch, "E161", {"start": v(-82.3, 44.63) * mm, "end": v(-62.17, 44.63) * mm});
            skLineSegment(sketch, "E162", {"start": v(-82.3, 41.78) * mm, "end": v(-60.63, 41.78) * mm});
            skLineSegment(sketch, "E163", {"start": v(-82.3, 39.01) * mm, "end": v(-59.13, 39.01) * mm});
            skLineSegment(sketch, "E164", {"start": v(-82.3, 36.2) * mm, "end": v(-57.62, 36.2) * mm});
            skLineSegment(sketch, "E165.0", {"start": v(-75.2, 66.63) * mm, "end": v(-82.96, 73.3) * mm});
            skLineSegment(sketch, "E165.1", {"start": v(-57.29, 33.5) * mm, "end": v(-75.2, 66.63) * mm});
            skLineSegment(sketch, "E166", {"start": v(-82.3, 74.07) * mm, "end": v(-82.3, 72.75) * mm});
            skLineSegment(sketch, "E167", {"start": v(-56.4, 33.97) * mm, "end": v(-57.55, 33.97) * mm});
            skSolve(sketch);
        }
        {
            var Q0;
            {var subQ3=sQuery(id+"F18.wireOp",EDGE,"E165.0");var subQ5=sQuery(id+"F18.wireOp",EDGE,"E165.1");var subQ7=makeQuery(id+"F18.imprint","INTERSECT",VERTEX,{"derivedFrom":[subQ3,subQ5]});Q0=makeQuery(id+"F18.imprint","IMPRINT",FACE,{"disambiguationData":[TD([[makeQuery(id+"F18.imprint","IMPRINT",EDGE,{"disambiguationData":[TD([[subQ7,1.0]])],"derivedFrom":subQ5}),1.0]])]});}
            var Q1;
            {var subQ0=sQuery(id+"F18.wireOp",EDGE,"E152.0");Q1=makeQuery(id+"F18.imprint","IMPRINT",FACE,{"disambiguationData":[TD([[makeQuery(id+"F18.imprint","IMPRINT",EDGE,{"derivedFrom":subQ0}),1.0]])]});}
            var Q2;
            {var subQ0=sQuery(id+"F18.wireOp",EDGE,"E160");Q2=makeQuery(id+"F18.imprint","IMPRINT",FACE,{"disambiguationData":[TD([[makeQuery(id+"F18.imprint","IMPRINT",EDGE,{"derivedFrom":subQ0}),-1.0]])]});}
            var Q3;
            {var subQ0=sQuery(id+"F18.wireOp",EDGE,"E159");Q3=makeQuery(id+"F18.imprint","IMPRINT",FACE,{"disambiguationData":[TD([[makeQuery(id+"F18.imprint","IMPRINT",EDGE,{"derivedFrom":subQ0}),-1.0]])]});}
            var Q4;
            {var subQ0=sQuery(id+"F18.wireOp",EDGE,"E158");Q4=makeQuery(id+"F18.imprint","IMPRINT",FACE,{"disambiguationData":[TD([[makeQuery(id+"F18.imprint","IMPRINT",EDGE,{"derivedFrom":subQ0}),-1.0]])]});}
            var Q5;
            {var subQ0=sQuery(id+"F18.wireOp",EDGE,"E157");Q5=makeQuery(id+"F18.imprint","IMPRINT",FACE,{"disambiguationData":[TD([[makeQuery(id+"F18.imprint","IMPRINT",EDGE,{"derivedFrom":subQ0}),-1.0]])]});}
            extrude(context, id + "F19", {"entities" : qUnion([Q0, Q1, Q2, Q3, Q4, Q5]), "operationType" : NewBodyOperationType.ADD, "depth" : 4 * mm, "offsetDistance" : 25 * mm});
        }
        {
            var Q0;
            Q0=makeQuery(id+"F19.opExtrude","CAP_FACE",FACE,{"disambiguationData":[OSD([sQuery(id+"F18.wireOp",EDGE,"E149.0"),sQuery(id+"F18.wireOp",EDGE,"E151.0"),sQuery(id+"F18.wireOp",EDGE,"E152.0"),sQuery(id+"F18.wireOp",EDGE,"E157"),sQuery(id+"F18.wireOp",EDGE,"E158"),sQuery(id+"F18.wireOp",EDGE,"E159"),sQuery(id+"F18.wireOp",EDGE,"E160"),sQuery(id+"F18.wireOp",EDGE,"E165.0"),sQuery(id+"F18.wireOp",EDGE,"E165.1")])],"isStart":false});
            extrude(context, id + "F20", {"entities" : qUnion([Q0]), "operationType" : NewBodyOperationType.REMOVE, "oppositeDirection" : true, "depth" : 2 * mm, "offsetDistance" : 25 * mm});
        }
        {
            var Q0;
            {var subQ7=sQuery(id+"F18.wireOp",EDGE,"E155");Q0=makeQuery(id+"F18.imprint","IMPRINT",FACE,{"disambiguationData":[TD([[makeQuery(id+"F18.imprint","IMPRINT",EDGE,{"derivedFrom":subQ7}),1.0]])]});}
            var Q1;
            {var subQ3=sQuery(id+"F18.wireOp",EDGE,"E165.1");var subQ5=sQuery(id+"F18.wireOp",EDGE,"E156");var subQ8=makeQuery(id+"F18.imprint","INTERSECT",VERTEX,{"derivedFrom":[subQ5,subQ3]});Q1=makeQuery(id+"F18.imprint","IMPRINT",FACE,{"disambiguationData":[TD([[makeQuery(id+"F18.imprint","IMPRINT",EDGE,{"disambiguationData":[TD([[subQ8,1.0]])],"derivedFrom":subQ5}),1.0]])]});}
            var Q2;
            {var subQ0=sQuery(id+"F18.wireOp",EDGE,"E161");var subQ1=sQuery(id+"F18.wireOp",EDGE,"E154");var subQ2=makeQuery(id+"F18.imprint","INTERSECT",VERTEX,{"derivedFrom":[subQ1,subQ0]});Q2=makeQuery(id+"F18.imprint","IMPRINT",FACE,{"disambiguationData":[TD([[makeQuery(id+"F18.imprint","IMPRINT",EDGE,{"disambiguationData":[TD([[subQ2,1.0]])],"derivedFrom":subQ1}),1.0]])]});}
            var Q3;
            {var subQ0=sQuery(id+"F18.wireOp",EDGE,"E162");var subQ1=sQuery(id+"F18.wireOp",EDGE,"E154");var subQ2=makeQuery(id+"F18.imprint","INTERSECT",VERTEX,{"derivedFrom":[subQ1,subQ0]});Q3=makeQuery(id+"F18.imprint","IMPRINT",FACE,{"disambiguationData":[TD([[makeQuery(id+"F18.imprint","IMPRINT",EDGE,{"disambiguationData":[TD([[subQ2,1.0]])],"derivedFrom":subQ1}),1.0]])]});}
            var Q4;
            {var subQ0=sQuery(id+"F18.wireOp",EDGE,"E163");var subQ1=sQuery(id+"F18.wireOp",EDGE,"E154");var subQ2=makeQuery(id+"F18.imprint","INTERSECT",VERTEX,{"derivedFrom":[subQ1,subQ0]});Q4=makeQuery(id+"F18.imprint","IMPRINT",FACE,{"disambiguationData":[TD([[makeQuery(id+"F18.imprint","IMPRINT",EDGE,{"disambiguationData":[TD([[subQ2,1.0]])],"derivedFrom":subQ1}),1.0]])]});}
            var Q5;
            {var subQ0=sQuery(id+"F18.wireOp",EDGE,"E167");Q5=makeQuery(id+"F18.imprint","IMPRINT",FACE,{"disambiguationData":[TD([[makeQuery(id+"F18.imprint","IMPRINT",EDGE,{"derivedFrom":subQ0}),-1.0]])]});}
            extrude(context, id + "F21", {"entities" : qUnion([Q0, Q1, Q2, Q3, Q4, Q5]), "operationType" : NewBodyOperationType.ADD, "depth" : 3 * mm, "offsetDistance" : 25 * mm});
        }
        {
            var Q0;
            {var subQ3=sQuery(id+"F15.wireOp",EDGE,"E142.0");var subQ5=sQuery(id+"F15.wireOp",EDGE,"E142.1");var subQ7=makeQuery(id+"F15.imprint","INTERSECT",VERTEX,{"derivedFrom":[subQ3,subQ5]});Q0=makeQuery(id+"F15.imprint","IMPRINT",FACE,{"disambiguationData":[TD([[makeQuery(id+"F15.imprint","IMPRINT",EDGE,{"disambiguationData":[TD([[subQ7,1.0]])],"derivedFrom":subQ5}),-1.0]])]});}
            var Q1;
            {var subQ0=sQuery(id+"F15.wireOp",EDGE,"E132.0");Q1=makeQuery(id+"F15.imprint","IMPRINT",FACE,{"disambiguationData":[TD([[makeQuery(id+"F15.imprint","IMPRINT",EDGE,{"derivedFrom":subQ0}),1.0]])]});}
            var Q2;
            {var subQ1=sQuery(id+"F15.wireOp",EDGE,"E131.0");var subQ3=sQuery(id+"F15.wireOp",EDGE,"E137.0");var subQ4=makeQuery(id+"F15.imprint","INTERSECT",VERTEX,{"derivedFrom":[subQ1,subQ3]});Q2=makeQuery(id+"F15.imprint","IMPRINT",FACE,{"disambiguationData":[TD([[makeQuery(id+"F15.imprint","IMPRINT",EDGE,{"disambiguationData":[TD([[subQ4,-1.0]])],"derivedFrom":subQ3}),-1.0]])]});}
            var Q3;
            {var subQ0=sQuery(id+"F15.wireOp",EDGE,"E137.0");var subQ1=sQuery(id+"F15.wireOp",EDGE,"E131.0");var subQ2=makeQuery(id+"F15.imprint","INTERSECT",VERTEX,{"derivedFrom":[subQ1,subQ0]});Q3=makeQuery(id+"F15.imprint","IMPRINT",FACE,{"disambiguationData":[TD([[makeQuery(id+"F15.imprint","IMPRINT",EDGE,{"disambiguationData":[TD([[subQ2,-1.0]])],"derivedFrom":subQ1}),-1.0]])]});}
            var Q4;
            {var subQ0=sQuery(id+"F15.wireOp",EDGE,"E138.0");var subQ1=sQuery(id+"F15.wireOp",EDGE,"E131.0");var subQ2=makeQuery(id+"F15.imprint","INTERSECT",VERTEX,{"derivedFrom":[subQ1,subQ0]});Q4=makeQuery(id+"F15.imprint","IMPRINT",FACE,{"disambiguationData":[TD([[makeQuery(id+"F15.imprint","IMPRINT",EDGE,{"disambiguationData":[TD([[subQ2,-1.0]])],"derivedFrom":subQ1}),-1.0]])]});}
            var Q5;
            {var subQ0=sQuery(id+"F15.wireOp",EDGE,"E139.0");var subQ1=sQuery(id+"F15.wireOp",EDGE,"E131.0");var subQ2=makeQuery(id+"F15.imprint","INTERSECT",VERTEX,{"derivedFrom":[subQ1,subQ0]});Q5=makeQuery(id+"F15.imprint","IMPRINT",FACE,{"disambiguationData":[TD([[makeQuery(id+"F15.imprint","IMPRINT",EDGE,{"disambiguationData":[TD([[subQ2,-1.0]])],"derivedFrom":subQ1}),-1.0]])]});}
            var Q6;
            {var subQ0=sQuery(id+"F15.wireOp",EDGE,"E131.0");var subQ1=sQuery(id+"F15.wireOp",EDGE,"E130.0");var subQ2=makeQuery(id+"F15.imprint","INTERSECT",VERTEX,{"derivedFrom":[subQ1,subQ0]});Q6=makeQuery(id+"F15.imprint","IMPRINT",FACE,{"disambiguationData":[TD([[makeQuery(id+"F15.imprint","IMPRINT",EDGE,{"disambiguationData":[TD([[subQ2,1.0]])],"derivedFrom":subQ0}),-1.0]])]});}
            extrude(context, id + "F22", {"entities" : qUnion([Q0, Q1, Q2, Q3, Q4, Q5, Q6]), "operationType" : NewBodyOperationType.ADD, "depth" : 2 * mm, "offsetDistance" : 25 * mm});
        }
        {
            var Q0;
            {var subQ0=sQuery(id+"F15.wireOp",EDGE,"E144");Q0=makeQuery(id+"F15.imprint","IMPRINT",FACE,{"disambiguationData":[TD([[makeQuery(id+"F15.imprint","IMPRINT",EDGE,{"derivedFrom":subQ0}),1.0]])]});}
            var Q1;
            {var subQ0=sQuery(id+"F15.wireOp",EDGE,"E139.0");var subQ1=sQuery(id+"F15.wireOp",EDGE,"E134");var subQ2=makeQuery(id+"F15.imprint","INTERSECT",VERTEX,{"derivedFrom":[subQ1,subQ0]});Q1=makeQuery(id+"F15.imprint","IMPRINT",FACE,{"disambiguationData":[TD([[makeQuery(id+"F15.imprint","IMPRINT",EDGE,{"disambiguationData":[TD([[subQ2,-1.0]])],"derivedFrom":subQ1}),-1.0]])]});}
            var Q2;
            {var subQ0=sQuery(id+"F15.wireOp",EDGE,"E140.0");var subQ1=sQuery(id+"F15.wireOp",EDGE,"E134");var subQ2=makeQuery(id+"F15.imprint","INTERSECT",VERTEX,{"derivedFrom":[subQ1,subQ0]});Q2=makeQuery(id+"F15.imprint","IMPRINT",FACE,{"disambiguationData":[TD([[makeQuery(id+"F15.imprint","IMPRINT",EDGE,{"disambiguationData":[TD([[subQ2,-1.0]])],"derivedFrom":subQ1}),-1.0]])]});}
            var Q3;
            {var subQ0=sQuery(id+"F15.wireOp",EDGE,"E138.0");var subQ1=sQuery(id+"F15.wireOp",EDGE,"E134");var subQ2=makeQuery(id+"F15.imprint","INTERSECT",VERTEX,{"derivedFrom":[subQ1,subQ0]});Q3=makeQuery(id+"F15.imprint","IMPRINT",FACE,{"disambiguationData":[TD([[makeQuery(id+"F15.imprint","IMPRINT",EDGE,{"disambiguationData":[TD([[subQ2,-1.0]])],"derivedFrom":subQ1}),-1.0]])]});}
            var Q4;
            {var subQ5=sQuery(id+"F15.wireOp",EDGE,"E136.0");var subQ6=sQuery(id+"F15.wireOp",EDGE,"E128.0");var subQ7=makeQuery(id+"F15.imprint","INTERSECT",VERTEX,{"derivedFrom":[subQ6,subQ5]});Q4=makeQuery(id+"F15.imprint","IMPRINT",FACE,{"disambiguationData":[TD([[makeQuery(id+"F15.imprint","IMPRINT",EDGE,{"disambiguationData":[TD([[subQ7,-1.0]])],"derivedFrom":subQ6}),1.0]])]});}
            var Q5;
            {var subQ4=sQuery(id+"F15.wireOp",EDGE,"E141");Q5=makeQuery(id+"F15.imprint","IMPRINT",FACE,{"disambiguationData":[TD([[makeQuery(id+"F15.imprint","IMPRINT",EDGE,{"derivedFrom":subQ4}),-1.0]])]});}
            extrude(context, id + "F23", {"entities" : qUnion([Q0, Q1, Q2, Q3, Q4, Q5]), "operationType" : NewBodyOperationType.ADD, "depth" : 3 * mm, "offsetDistance" : 25 * mm});
        }
        {
            var Q0;
            {var subQ5=sQuery(id+"F15.wireOp",EDGE,"E136.0");var subQ6=sQuery(id+"F15.wireOp",EDGE,"E128.0");var subQ7=makeQuery(id+"F15.imprint","INTERSECT",VERTEX,{"derivedFrom":[subQ6,subQ5]});Q0=makeQuery(id+"F15.imprint","IMPRINT",FACE,{"disambiguationData":[TD([[makeQuery(id+"F15.imprint","IMPRINT",EDGE,{"disambiguationData":[TD([[subQ7,-1.0]])],"derivedFrom":subQ6}),-1.0]])]});}
            extrude(context, id + "F24", {"entities" : qUnion([Q0]), "operationType" : NewBodyOperationType.ADD, "depth" : 3 * mm, "offsetDistance" : 25 * mm});
        }
    });
